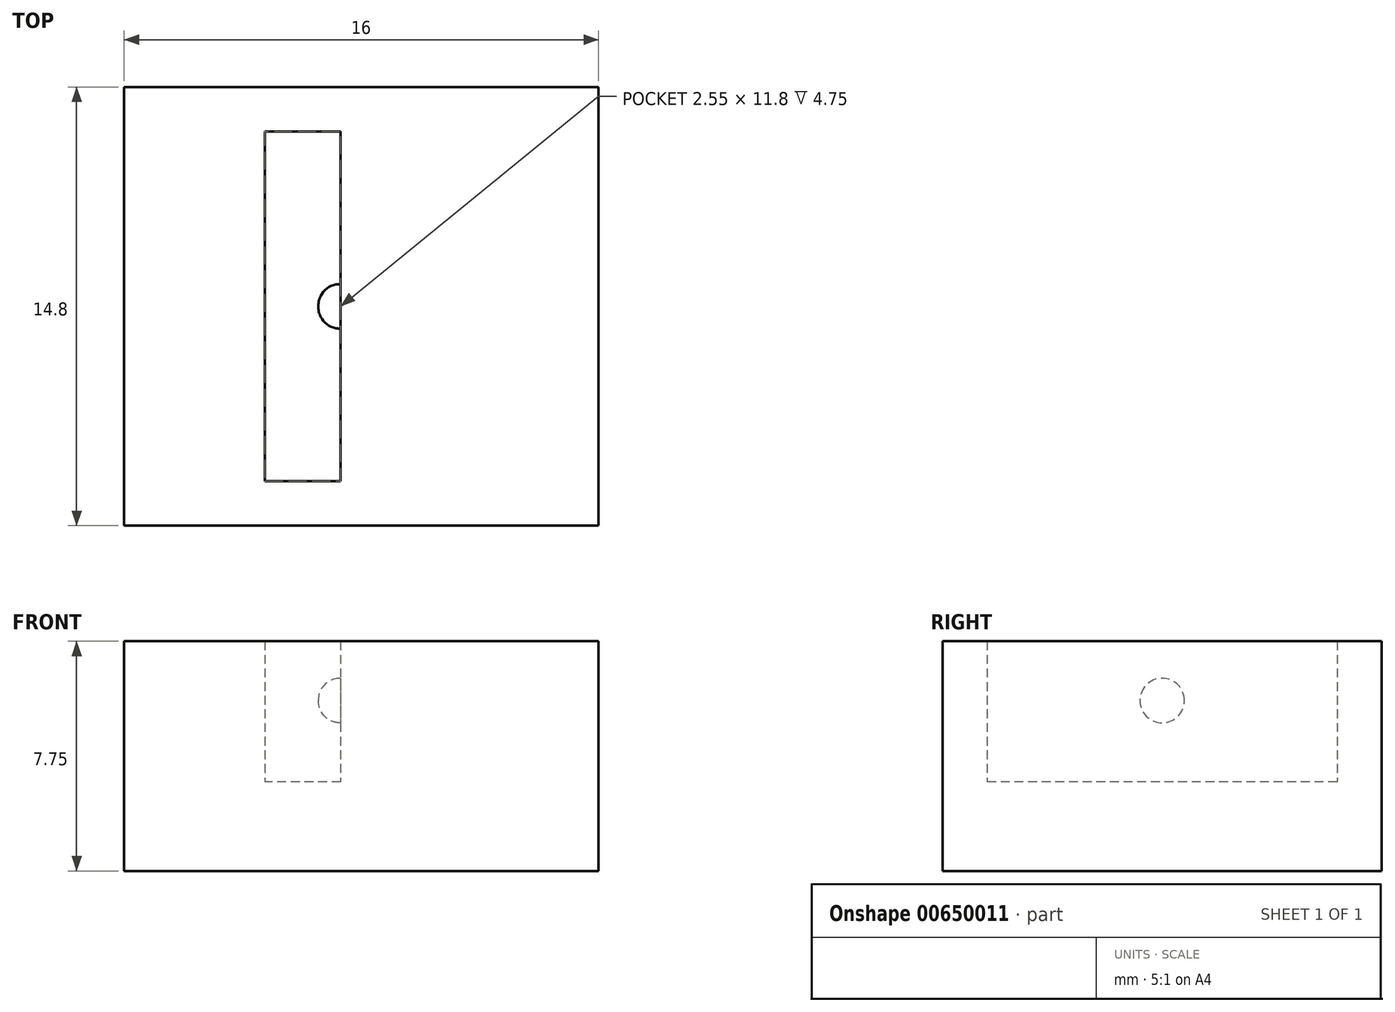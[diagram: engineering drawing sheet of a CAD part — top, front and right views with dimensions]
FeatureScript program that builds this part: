
annotation { "Feature Type Name" : "Feature", "Feature Type Description" : "" }
export const myFeature = defineFeature(function(context is Context, id is Id, definition is map)
    precondition{}
    {
        {
            assignVariable(context, id + "F0", {"name" : "tab_depth", "anyValue" : 4.75});
        }
        {
            assignVariable(context, id + "F1", {"name" : "notch_depth", "anyValue" : .75});
        }
        {
            assignVariable(context, id + "F2", {"name" : "base_depth", "anyValue" : 3});
        }
        {
            var Q0;
            Q0=qCreatedBy(makeId("Top.planeOp"),FACE);
            var sketch = newSketch(context, id + "F3", { "sketchPlane" : qUnion([Q0])});
            skLineSegment(sketch, "E0.bottom", {"start": v(8, -5.9) * mm, "end": v(-8, -5.9) * mm});
            skLineSegment(sketch, "E0.top", {"start": v(8, 5.9) * mm, "end": v(-8, 5.9) * mm});
            skLineSegment(sketch, "E0.left", {"start": v(8, -5.9) * mm, "end": v(8, 5.9) * mm});
            skLineSegment(sketch, "E0.right", {"start": v(-8, -5.9) * mm, "end": v(-8, 5.9) * mm});
            skPoint(sketch, "E0.middle", {"position": v(0, 0) * mm});
            skLineSegment(sketch, "E1.bottom", {"start": v(-0.7, -5.9) * mm, "end": v(-3.25, -5.9) * mm});
            skLineSegment(sketch, "E1.top", {"start": v(-0.7, 5.9) * mm, "end": v(-3.25, 5.9) * mm});
            skLineSegment(sketch, "E1.left", {"start": v(-0.7, -5.9) * mm, "end": v(-0.7, 5.9) * mm});
            skLineSegment(sketch, "E1.right", {"start": v(-3.25, -5.9) * mm, "end": v(-3.25, 5.9) * mm});
            skLineSegment(sketch, "E2", {"start": v(-8, 0) * mm, "end": v(-3.25, 0) * mm, "construction": true});
            skLineSegment(sketch, "E3.bottom", {"start": v(-8, 5.9) * mm, "end": v(8, 5.9) * mm});
            skLineSegment(sketch, "E3.top", {"start": v(-8, 7.4) * mm, "end": v(8, 7.4) * mm});
            skLineSegment(sketch, "E3.left", {"start": v(-8, 5.9) * mm, "end": v(-8, 7.4) * mm});
            skLineSegment(sketch, "E3.right", {"start": v(8, 5.9) * mm, "end": v(8, 7.4) * mm});
            skLineSegment(sketch, "E4.bottom", {"start": v(-8, -5.9) * mm, "end": v(8, -5.9) * mm});
            skLineSegment(sketch, "E4.top", {"start": v(-8, -7.4) * mm, "end": v(8, -7.4) * mm});
            skLineSegment(sketch, "E4.left", {"start": v(-8, -5.9) * mm, "end": v(-8, -7.4) * mm});
            skLineSegment(sketch, "E4.right", {"start": v(8, -5.9) * mm, "end": v(8, -7.4) * mm});
            skSolve(sketch);
        }
        {
            var Q0;
            {var subQ0=sQuery(id+"F3.wireOp",EDGE,"E0.left");Q0=makeQuery(id+"F3.imprint","IMPRINT",FACE,{"disambiguationData":[TD([[makeQuery(id+"F3.imprint","IMPRINT",EDGE,{"derivedFrom":subQ0}),1.0]])]});}
            var Q1;
            Q1=makeQuery(id+"F3.imprint","IMPRINT",FACE,{"disambiguationData":[TD([[makeQuery(id+"F3.imprint","IMPRINT",EDGE,{"derivedFrom":sQuery(id+"F3.wireOp",EDGE,"E1.bottom")}),-1.0]])]});
            var Q2;
            {var subQ0=sQuery(id+"F3.wireOp",EDGE,"E0.right");Q2=makeQuery(id+"F3.imprint","IMPRINT",FACE,{"disambiguationData":[TD([[makeQuery(id+"F3.imprint","IMPRINT",EDGE,{"derivedFrom":subQ0}),-1.0]])]});}
            var Q3;
            {var subQ0=sQuery(id+"F3.wireOp",EDGE,"E1.left");Q3=makeQuery(id+"F3.imprint","IMPRINT",FACE,{"disambiguationData":[TD([[makeQuery(id+"F3.imprint","IMPRINT",EDGE,{"derivedFrom":subQ0}),1.0]])]});}
            extrude(context, id + "F4", {"entities" : qUnion([Q0, Q1, Q2, Q3]), "depth" : (getVariable(context, 'base_depth')) * mm, "offsetDistance" : 25 * mm});
        }
        {
            var Q0;
            {var subQ0=sQuery(id+"F3.wireOp",EDGE,"E0.left");Q0=makeQuery(id+"F3.imprint","IMPRINT",FACE,{"disambiguationData":[TD([[makeQuery(id+"F3.imprint","IMPRINT",EDGE,{"derivedFrom":subQ0}),1.0]])]});}
            var Q1;
            Q1=makeQuery(id+"F3.imprint","IMPRINT",FACE,{"disambiguationData":[TD([[makeQuery(id+"F3.imprint","IMPRINT",EDGE,{"derivedFrom":sQuery(id+"F3.wireOp",EDGE,"79MO9lO9-fJW3-r8wz-jZY0-4If8DLmvSZgb")}),1.0]])]});
            var Q2;
            Q2=makeQuery(id+"F3.imprint","IMPRINT",FACE,{"disambiguationData":[TD([[makeQuery(id+"F3.imprint","IMPRINT",EDGE,{"derivedFrom":sQuery(id+"F3.wireOp",EDGE,"E4.top")}),1.0]])]});
            var Q3;
            Q3=makeQuery(id+"F3.imprint","IMPRINT",FACE,{"disambiguationData":[TD([[makeQuery(id+"F3.imprint","IMPRINT",EDGE,{"derivedFrom":sQuery(id+"F3.wireOp",EDGE,"E3.top")}),-1.0]])]});
            extrude(context, id + "F5", {"entities" : qUnion([Q0, Q1, Q2, Q3]), "operationType" : NewBodyOperationType.ADD, "depth" : (getVariable(context, 'base_depth') + getVariable(context, 'tab_depth')) * mm, "offsetDistance" : 25 * mm});
        }
        {
            var Q0;
            Q0=makeQuery(id+"F5.opExtrude","SWEPT_FACE",FACE,{"disambiguationData":[OSD([sQuery(id+"F3.wireOp",EDGE,"E1.left")])]});
            var sketch = newSketch(context, id + "F6", { "sketchPlane" : qUnion([Q0])});
            skLineSegment(sketch, "E5", {"start": v(0, 7.75) * mm, "end": v(0, 5.75) * mm, "construction": true});
            skCircle(sketch, "E6", {"center": v(0, 5.75) * mm, "radius": 0.75 * mm});
            skSolve(sketch);
        }
        {
            var Q0;
            Q0=makeQuery(id+"F6.imprint","IMPRINT",FACE,{"disambiguationData":[TD([[makeQuery(id+"F6.imprint","IMPRINT",EDGE,{"derivedFrom":sQuery(id+"F6.wireOp",EDGE,"E6")}),1.0]])]});
            extrude(context, id + "F7", {"entities" : qUnion([Q0]), "operationType" : NewBodyOperationType.ADD, "depth" : (getVariable(context, 'notch_depth')) * mm, "offsetDistance" : 25 * mm});
        }
        {
            var Q0;
            Q0=makeQuery(id+"F7.opExtrude","CAP_EDGE",EDGE,{"disambiguationData":[OSD([sQuery(id+"F6.wireOp",EDGE,"E6")])],"isStart":false});
            fillet(context, id + "F8", {"entities" : qUnion([Q0]), "radius" : 0.72 * mm, "tangentPropagation" : true, "allowEdgeOverflow" : false});
        }
        {
            var Q0;
            {var subQ0=sQuery(id+"F3.wireOp",EDGE,"E0.right");Q0=makeQuery(id+"F3.imprint","IMPRINT",FACE,{"disambiguationData":[TD([[makeQuery(id+"F3.imprint","IMPRINT",EDGE,{"derivedFrom":subQ0}),-1.0]])]});}
            extrude(context, id + "F9", {"entities" : qUnion([Q0]), "operationType" : NewBodyOperationType.ADD, "depth" : (getVariable(context, 'base_depth') + getVariable(context, 'tab_depth')) * mm, "offsetDistance" : 25 * mm});
        }
    });
